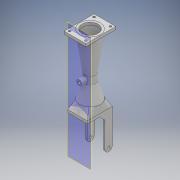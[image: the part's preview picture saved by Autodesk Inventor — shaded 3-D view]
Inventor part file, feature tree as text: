
AUTODESK INVENTOR PART (.ipt)
format: ipt  version: 2017 (Build 210142000, 142)  size: 395,264 bytes
history: native  units: mm
features: sketch x8, extrude x5, plane x4, projected_geometry x3, loft x2, other x2, revolve x1, fillet x1, chamfer x1, mirror x1
ambient origin geometry x8: Origin, YZ Plane, XZ Plane, XY Plane, X Axis, Y Axis, Z Axis, Center Point
bodies: Solid1 (feature_tree)
feature tree (28):
  extrude  "Extrusion1"  Depth=30.0mm
  plane  "Work Plane1"
  sketch  "Sketch2"  dims[d2=3.0mm d3=3.0mm]
  sketch  "Sketch3"  dims[d4=5.0mm d5=0.0mm d6=15.0mm]
  loft  "Loft1"
  loft  "Loft2"
  revolve  "Revolution1"  [1 undecoded]
  plane  "Work Plane3"
  extrude  "Extrusion2"  TaperAngle=0.0deg  [1 undecoded]
  fillet  "Fillet1"  [1 undecoded]
  extrude  "Extrusion3"  Depth=15.0mm
  chamfer  "Chamfer1"  Distance=5.0mm
  mirror  "Mirror1"
  extrude  "Extrusion4"  Depth=10.0mm
  plane  "Work Plane4"
  extrude  "Extrusion5"  Depth=10.0mm
  sketch  "Sketch1"  dims[d0=40.0mm d1=30.0mm]
  projected_geometry  "Projected Loop1"
  other  "Edges1"
  other  "Edges2"
  sketch  "Sketch5"  dims[d7=30.0mm d8=4.0mm]
  plane  "Work Plane2"
  sketch  "Sketch6"  dims[d9=0.0mm d10=90.0deg d11=0.0mm d12=90.0deg d13=0.0mm d14=90.0deg]
  sketch  "Sketch7"  dims[d15=0.0mm d16=90.0deg d19=15.0mm]
  projected_geometry  "Projected Loop3"
  sketch  "Sketch8"  dims[d20=4.0mm]
  sketch  "Sketch9"  dims[d22=3.490659mm d23=5.0mm d24=1.396263mm d25=8.0mm d26=15.0mm d27=5.0mm d28=4.0mm d29=5.0mm d30=5.0mm d31=4.0mm d32=90.0deg d33=5.0mm d34=55.0mm d35=40.0mm d36=4.0mm d37=45.0mm d38=30.0mm d39=5.0mm d40=0.0mm d41=30.0mm d42=62.0mm d43=36.2mm d44=4.5mm d45=6.0mm d46=0.0mm d47=10.0mm d48=2.0mm d49=45.0deg d50=5.0mm d51=6.0mm d52=0.0mm d53=-20.0mm d54=10.0mm d55=6.0mm d56=0.0mm]
  projected_geometry  "Projected Loop4"
note: 3 required parameter values undecoded (feature->parameter linkage not recoverable at this tier; creation-order binding heuristic only, values carry confidence <= 0.55)